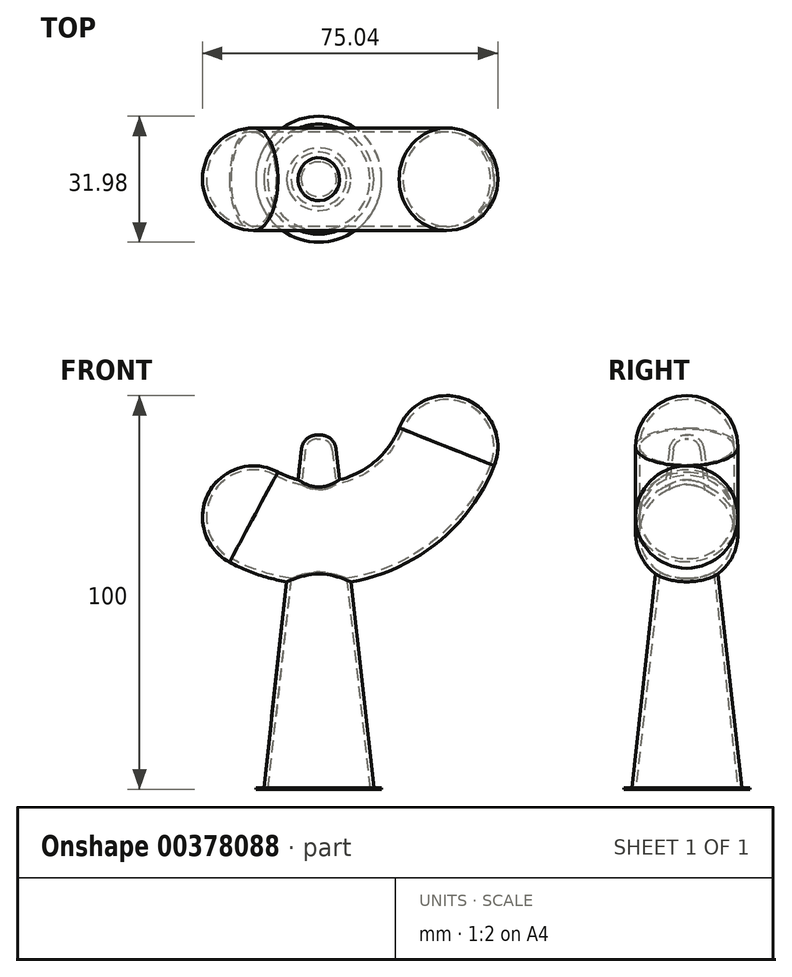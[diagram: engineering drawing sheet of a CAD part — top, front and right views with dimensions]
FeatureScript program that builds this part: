
annotation { "Feature Type Name" : "Feature", "Feature Type Description" : "" }
export const myFeature = defineFeature(function(context is Context, id is Id, definition is map)
    precondition{}
    {
        {
            var Q0;
            Q0=qCreatedBy(makeId("Front.planeOp"),FACE);
            var sketch = newSketch(context, id + "F0", { "sketchPlane" : qUnion([Q0])});
            skLineSegment(sketch, "E0", {"start": v(0, 0) * mm, "end": v(0, 90) * mm});
            skArc(sketch, "E1", {"start": v(-26.81, 77.5) * mm, "mid": v(11.97, 67.11) * mm, "end": v(35, 100) * mm});
            skPoint(sketch, "E2", {"position": v(0, 90) * mm});
            skLineSegment(sketch, "E3", {"start": v(-14, 0) * mm, "end": v(0, 0) * mm});
            skLineSegment(sketch, "E4", {"start": v(0, 90) * mm, "end": v(-4, 90) * mm});
            skLineSegment(sketch, "E5", {"start": v(-4, 90) * mm, "end": v(-14, 0) * mm});
            skLineSegment(sketch, "E6", {"start": v(0, 90) * mm, "end": v(0, 100) * mm, "construction": true});
            skLineSegment(sketch, "E7", {"start": v(0, 100) * mm, "end": v(35, 100) * mm, "construction": true});
            skLineSegment(sketch, "E8", {"start": v(0, 100) * mm, "end": v(-26.81, 77.5) * mm, "construction": true});
            skSolve(sketch);
        }
        {
            var Q0;
            Q0=sQuery(id+"F0.wireOp",VERTEX,"E1.end");
            var Q1;
            Q1=sQuery(id+"F0.wireOp",EDGE,"E1");
            cPlane(context, id + "F1", {"entities" : qUnion([Q0, Q1]), "cplaneType" : CPlaneType.CURVE_POINT, "offset" : 25 * mm, "width" : 150 * mm, "height" : 150 * mm});
        }
        {
            var Q0;
            Q0=qCreatedBy(id+"F1.planeOp",FACE);
            var sketch = newSketch(context, id + "F2", { "sketchPlane" : qUnion([Q0])});
            skPoint(sketch, "E9.0", {"position": v(35, 0) * mm});
            skCircle(sketch, "E10", {"center": v(35, 0) * mm, "radius": 13 * mm});
            skSolve(sketch);
        }
        {
            var Q0;
            Q0=makeQuery(id+"F2.imprint","IMPRINT",FACE,{"disambiguationData":[TD([[makeQuery(id+"F2.imprint","IMPRINT",EDGE,{"derivedFrom":sQuery(id+"F2.wireOp",EDGE,"E10")}),1.0]])]});
            var Q1;
            Q1=sQuery(id+"F0.wireOp",EDGE,"E1");
            sweep(context, id + "F3", {"profiles" : qUnion([Q0]), "path" : qUnion([Q1])});
        }
        {
            var Q0;
            {var subQ0=sQuery(id+"F0.wireOp",EDGE,"E3");Q0=makeQuery(id+"F0.imprint","IMPRINT",FACE,{"disambiguationData":[TD([[makeQuery(id+"F0.imprint","IMPRINT",EDGE,{"derivedFrom":subQ0}),1.0]])]});}
            var Q1;
            {var subQ0=sQuery(id+"F0.wireOp",EDGE,"E4");Q1=makeQuery(id+"F0.imprint","IMPRINT",FACE,{"disambiguationData":[TD([[makeQuery(id+"F0.imprint","IMPRINT",EDGE,{"derivedFrom":subQ0}),1.0]])]});}
            var Q2;
            Q2=sQuery(id+"F0.wireOp",EDGE,"E0");
            revolve(context, id + "F4", {"operationType" : NewBodyOperationType.ADD, "entities" : qUnion([Q0, Q1]), "axis" : qUnion([Q2]), "revolveType" : RevolveType.FULL});
        }
        {
            var Q0;
            Q0=makeQuery(id+"F3.opSweep","CAP_FACE",FACE,{"disambiguationData":[OSD([sQuery(id+"F0.wireOp",VERTEX,"E1.start"),sQuery(id+"F2.wireOp",EDGE,"E10")])],"isStart":false});
            var Q1;
            Q1=makeQuery(id+"F3.opSweep","CAP_FACE",FACE,{"disambiguationData":[OSD([sQuery(id+"F0.wireOp",VERTEX,"E1.end"),sQuery(id+"F2.wireOp",EDGE,"E10")])],"isStart":true});
            fillet(context, id + "F5", {"entities" : qUnion([Q0, Q1]), "radius" : 13 * mm, "tangentPropagation" : true, "allowEdgeOverflow" : false});
        }
        {
            var Q0;
            Q0=makeQuery(id+"F4.opRevolve","SWEPT_EDGE",EDGE,{"disambiguationData":[OSD([sQuery(id+"F0.wireOp",EDGE,"E4"),sQuery(id+"F0.wireOp",EDGE,"E5")])]});
            fillet(context, id + "F6", {"entities" : qUnion([Q0]), "radius" : 4 * mm, "tangentPropagation" : true, "allowEdgeOverflow" : false});
        }
        {
            var Q0;
            Q0=makeQuery(id+"F4.opRevolve","SWEPT_FACE",FACE,{"disambiguationData":[OSD([sQuery(id+"F0.wireOp",EDGE,"E3")])]});
            shell(context, id + "F7", {"entities" : qUnion([Q0]), "thickness" : 1 * mm});
        }
        {
            var Q0;
            Q0=qCreatedBy(makeId("Top.planeOp"),FACE);
            var sketch = newSketch(context, id + "F8", { "sketchPlane" : qUnion([Q0])});
            skCircle(sketch, "E11.0", {"center": v(0, 0) * mm, "radius": 13 * mm});
            skCircle(sketch, "E12.0", {"center": v(0, 0) * mm, "radius": 16 * mm});
            skSolve(sketch);
        }
        {
            var Q0;
            Q0 = qSketchRegion(id + "F8", true);
            extrude(context, id + "F9", {"entities" : qUnion([Q0]), "operationType" : NewBodyOperationType.ADD, "depth" : .3 * mm});
        }
    });
